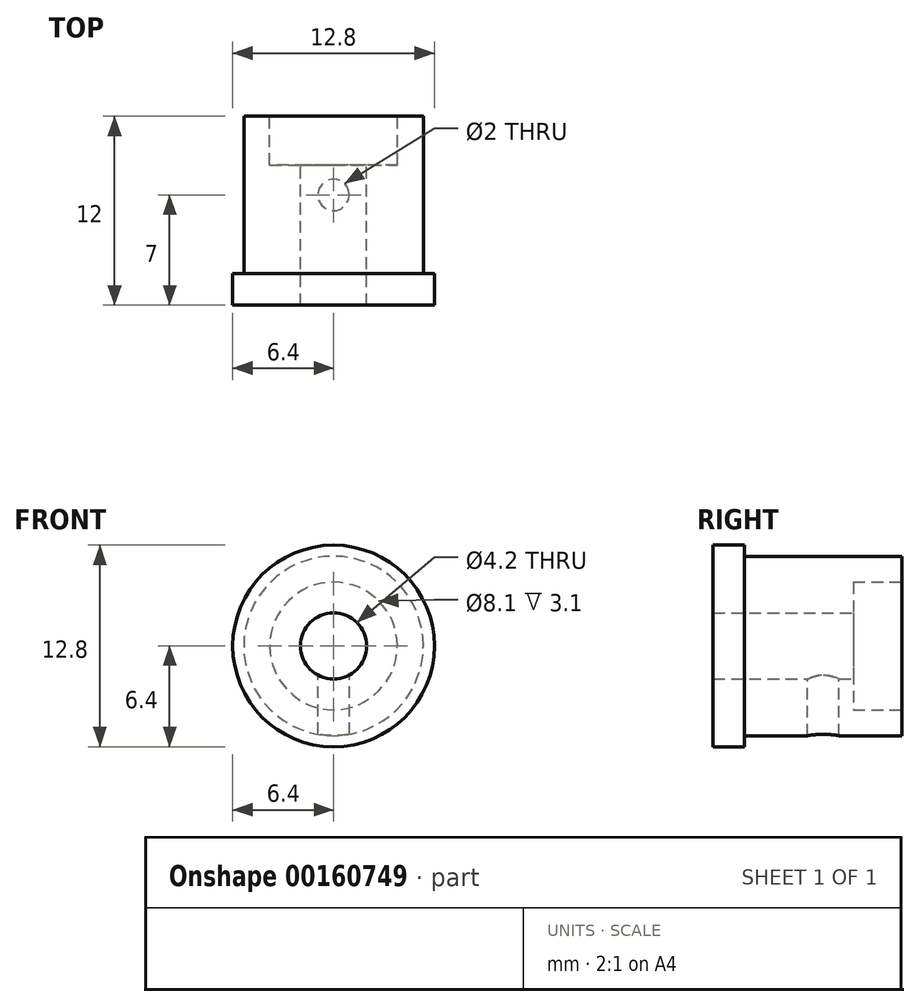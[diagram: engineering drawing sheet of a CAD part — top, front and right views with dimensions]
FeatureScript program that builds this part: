
annotation { "Feature Type Name" : "Feature", "Feature Type Description" : "" }
export const myFeature = defineFeature(function(context is Context, id is Id, definition is map)
    precondition{}
    {
        {
            assignVariable(context, id + "F0", {"name" : "InDiam_Bore", "anyValue" : 2});
        }
        {
            var Q0;
            Q0=qCreatedBy(makeId("Right.planeOp"),FACE);
            var sketch = newSketch(context, id + "F1", { "sketchPlane" : qUnion([Q0])});
            skLineSegment(sketch, "E0", {"start": v(11.47, 0) * mm, "end": v(0, 0) * mm, "construction": true});
            skLineSegment(sketch, "E1", {"start": v(8.9, 2.1) * mm, "end": v(0, 2.1) * mm});
            skLineSegment(sketch, "E2", {"start": v(8.9, 2.1) * mm, "end": v(8.9, 4.05) * mm});
            skLineSegment(sketch, "E3", {"start": v(12, 4.05) * mm, "end": v(8.9, 4.05) * mm});
            skLineSegment(sketch, "E4", {"start": v(12, 4.05) * mm, "end": v(12, 5.7) * mm});
            skLineSegment(sketch, "E5", {"start": v(2, 5.7) * mm, "end": v(12, 5.7) * mm});
            skLineSegment(sketch, "E6", {"start": v(2, 5.7) * mm, "end": v(2, 6.4) * mm});
            skLineSegment(sketch, "E7", {"start": v(0, 6.4) * mm, "end": v(2, 6.4) * mm});
            skLineSegment(sketch, "E8", {"start": v(0, 6.4) * mm, "end": v(0, 2.1) * mm});
            skSolve(sketch);
        }
        {
            var Q0;
            Q0=makeQuery(id+"F1.imprint","IMPRINT",FACE,{"disambiguationData":[TD([[makeQuery(id+"F1.imprint","IMPRINT",EDGE,{"derivedFrom":sQuery(id+"F1.wireOp",EDGE,"E1")}),-1.0]])]});
            var Q1;
            Q1=sQuery(id+"F1.wireOp",EDGE,"E0");
            revolve(context, id + "F2", {"entities" : qUnion([Q0]), "axis" : qUnion([Q1]), "revolveType" : RevolveType.FULL});
        }
        {
            var Q0;
            Q0=qCreatedBy(makeId("Top.planeOp"),FACE);
            var sketch = newSketch(context, id + "F3", { "sketchPlane" : qUnion([Q0])});
            skCircle(sketch, "E9", {"center": v(0, 7) * mm, "radius": 1 * mm});
            skLineSegment(sketch, "E10.0", {"start": v(-5.7, 12) * mm, "end": v(5.7, 12) * mm});
            skSolve(sketch);
        }
        {
            var Q0;
            Q0=sQuery(id+"F3.wireOp",VERTEX,"E9.center");
            var Q1;
            Q1=makeQuery(id+"F2.opRevolve","SWEPT_BODY",BODY,{"disambiguationData":[OSD([sQuery(id+"F1.wireOp",EDGE,"E1"),sQuery(id+"F1.wireOp",EDGE,"E2"),sQuery(id+"F1.wireOp",EDGE,"E3"),sQuery(id+"F1.wireOp",EDGE,"E4"),sQuery(id+"F1.wireOp",EDGE,"E5"),sQuery(id+"F1.wireOp",EDGE,"E6"),sQuery(id+"F1.wireOp",EDGE,"E7"),sQuery(id+"F1.wireOp",EDGE,"E8")])]});
            hole(context, id + "F4", {"style" : HoleStyle.SIMPLE, "endStyle" : HoleEndStyle.THROUGH, "holeDiameter" : (getVariable(context, 'InDiam_Bore')) * mm, "startFromSketch" : true, "locations" : qUnion([Q0]), "scope" : qUnion([Q1]), "isTappedThrough" : true});
        }
    });
